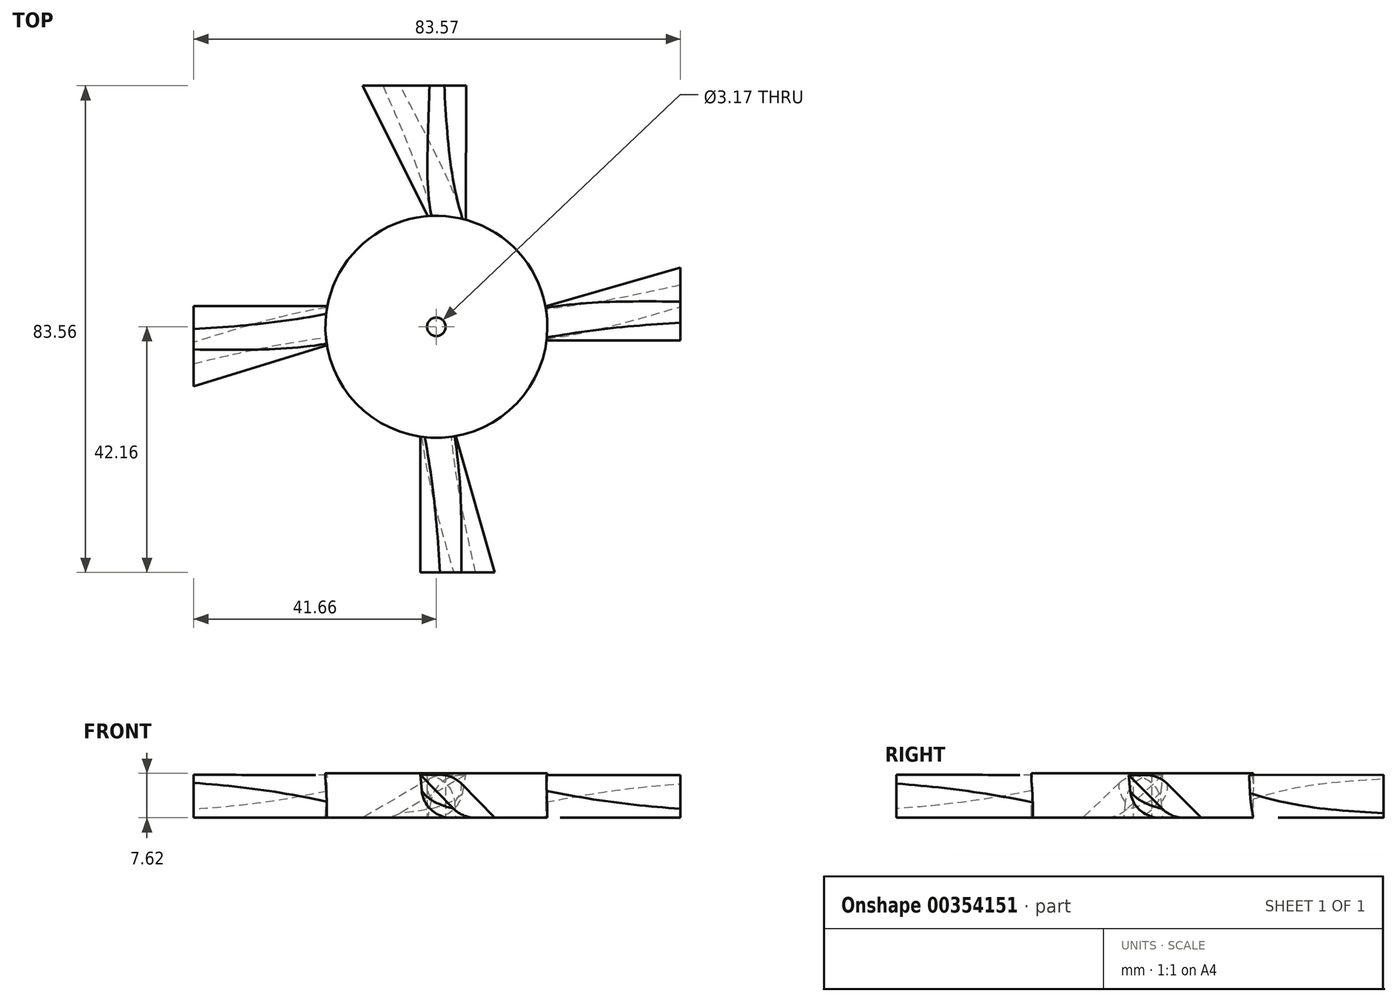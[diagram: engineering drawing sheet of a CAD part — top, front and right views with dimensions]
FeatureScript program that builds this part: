
annotation { "Feature Type Name" : "Feature", "Feature Type Description" : "" }
export const myFeature = defineFeature(function(context is Context, id is Id, definition is map)
    precondition{}
    {
        {
            var Q0;
            Q0=qCreatedBy(makeId("Top.planeOp"),FACE);
            var sketch = newSketch(context, id + "F0", { "sketchPlane" : qUnion([Q0])});
            skCircle(sketch, "E0", {"center": v(0, 0) * mm, "radius": 19.05 * mm});
            skCircle(sketch, "E1", {"center": v(0, 0) * mm, "radius": 1.59 * mm});
            skSolve(sketch);
        }
        {
            var Q0;
            Q0=makeQuery(id+"F0.imprint","IMPRINT",FACE,{"disambiguationData":[TD([[makeQuery(id+"F0.imprint","IMPRINT",EDGE,{"derivedFrom":sQuery(id+"F0.wireOp",EDGE,"E0")}),1.0]])]});
            extrude(context, id + "F1", {"entities" : qUnion([Q0]), "depth" : 7.62 * mm});
        }
        {
            var Q0;
            Q0=qCreatedBy(makeId("Front.planeOp"),FACE);
            cPlane(context, id + "F2", {"entities" : qUnion([Q0]), "cplaneType" : CPlaneType.OFFSET, "offset" : 16 * mm, "oppositeDirection" : true, "width" : 152.4 * mm, "height" : 152.4 * mm});
        }
        {
            var Q0;
            Q0=qCreatedBy(id+"F2.planeOp",FACE);
            var sketch = newSketch(context, id + "F3", { "sketchPlane" : qUnion([Q0])});
            skLineSegment(sketch, "E2.bottom", {"start": v(0, 7.29) * mm, "end": v(5.03, 7.29) * mm});
            skLineSegment(sketch, "E2.top", {"start": v(0, 0) * mm, "end": v(5.03, 0) * mm});
            skLineSegment(sketch, "E2.left", {"start": v(0, 7.29) * mm, "end": v(0, 0) * mm});
            skLineSegment(sketch, "E2.right", {"start": v(5.03, 7.29) * mm, "end": v(5.03, 0) * mm});
            skSolve(sketch);
        }
        {
            var Q0;
            Q0=qCreatedBy(id+"F2.planeOp",FACE);
            cPlane(context, id + "F4", {"entities" : qUnion([Q0]), "cplaneType" : CPlaneType.OFFSET, "offset" : 25.4 * mm, "oppositeDirection" : true, "width" : 152.4 * mm, "height" : 152.4 * mm});
        }
        {
            var Q0;
            Q0=qCreatedBy(id+"F4.planeOp",FACE);
            var sketch = newSketch(context, id + "F5", { "sketchPlane" : qUnion([Q0])});
            skLineSegment(sketch, "E3.bottom", {"start": v(5.1, 7.38) * mm, "end": v(0, 7.38) * mm});
            skLineSegment(sketch, "E3.top", {"start": v(-7.57, 0) * mm, "end": v(-12.68, 0) * mm});
            skLineSegment(sketch, "E3.left", {"start": v(5.1, 7.38) * mm, "end": v(-7.57, 0) * mm});
            skLineSegment(sketch, "E3.right", {"start": v(0, 7.38) * mm, "end": v(-12.68, 0) * mm});
            skSolve(sketch);
        }
        {
            var Q1;
            Q1 = qSketchRegion(id + "F3", true);
            var Q2;
            Q2 = qSketchRegion(id + "F5", true);
            loft(context, id + "F6", {"operationType" : NewBodyOperationType.ADD, "sheetProfilesArray" : [{ "sheetProfileEntities" : qUnion([Q1]) }, { "sheetProfileEntities" : qUnion([Q2]) }]});
        }
        {
            var Q0;
            Q0=makeQuery(id+"F6.opLoft","SWEPT_EDGE",EDGE,{"disambiguationData":[OSD([sQuery(id+"F3.wireOp",EDGE,"E2.bottom"),sQuery(id+"F3.wireOp",EDGE,"E2.left"),sQuery(id+"F5.wireOp",EDGE,"E3.bottom"),sQuery(id+"F5.wireOp",EDGE,"E3.right")])]});
            fillet(context, id + "F7", {"entities" : qUnion([Q0]), "radius" : 5.08 * mm, "tangentPropagation" : true, "allowEdgeOverflow" : false});
        }
        {
            var Q0;
            Q0=makeQuery(id+"F6.opLoft","SWEPT_EDGE",EDGE,{"disambiguationData":[OSD([sQuery(id+"F3.wireOp",EDGE,"E2.top"),sQuery(id+"F3.wireOp",EDGE,"E2.right"),sQuery(id+"F5.wireOp",EDGE,"E3.top"),sQuery(id+"F5.wireOp",EDGE,"E3.left")])]});
            fillet(context, id + "F8", {"entities" : qUnion([Q0]), "radius" : 5.08 * mm, "tangentPropagation" : true, "allowEdgeOverflow" : false});
        }
        {
            var Q0;
            Q0=qCreatedBy(makeId("Right.planeOp"),FACE);
            cPlane(context, id + "F9", {"entities" : qUnion([Q0]), "cplaneType" : CPlaneType.OFFSET, "offset" : 16.26 * mm, "oppositeDirection" : true, "width" : 152.4 * mm, "height" : 152.4 * mm});
        }
        {
            var Q0;
            Q0=qCreatedBy(id+"F9.planeOp",FACE);
            var sketch = newSketch(context, id + "F10", { "sketchPlane" : qUnion([Q0])});
            skLineSegment(sketch, "E4.bottom", {"start": v(3.55, 7.32) * mm, "end": v(-2.42, 7.32) * mm});
            skLineSegment(sketch, "E4.top", {"start": v(3.55, 0) * mm, "end": v(-2.42, 0) * mm});
            skLineSegment(sketch, "E4.left", {"start": v(3.55, 7.32) * mm, "end": v(3.55, 0) * mm});
            skLineSegment(sketch, "E4.right", {"start": v(-2.42, 7.32) * mm, "end": v(-2.42, 0) * mm});
            skSolve(sketch);
        }
        {
            var Q0;
            Q0=qCreatedBy(id+"F9.planeOp",FACE);
            cPlane(context, id + "F11", {"entities" : qUnion([Q0]), "cplaneType" : CPlaneType.OFFSET, "offset" : 25.4 * mm, "oppositeDirection" : true, "width" : 152.4 * mm, "height" : 152.4 * mm});
        }
        {
            var Q0;
            Q0=qCreatedBy(id+"F11.planeOp",FACE);
            var sketch = newSketch(context, id + "F12", { "sketchPlane" : qUnion([Q0])});
            skLineSegment(sketch, "E5.bottom", {"start": v(3.58, 7.37) * mm, "end": v(-2.42, 7.37) * mm});
            skLineSegment(sketch, "E5.top", {"start": v(-4.2, 0) * mm, "end": v(-10.2, 0) * mm});
            skLineSegment(sketch, "E5.left", {"start": v(3.58, 7.37) * mm, "end": v(-4.2, 0) * mm});
            skLineSegment(sketch, "E5.right", {"start": v(-2.42, 7.37) * mm, "end": v(-10.2, 0) * mm});
            skSolve(sketch);
        }
        {
            var Q1;
            Q1 = qSketchRegion(id + "F10", true);
            var Q2;
            Q2 = qSketchRegion(id + "F12", true);
            loft(context, id + "F13", {"operationType" : NewBodyOperationType.ADD, "sheetProfilesArray" : [{ "sheetProfileEntities" : qUnion([Q1]) }, { "sheetProfileEntities" : qUnion([Q2]) }]});
        }
        {
            var Q0;
            Q0=makeQuery(id+"F13.opLoft","SWEPT_EDGE",EDGE,{"disambiguationData":[OSD([sQuery(id+"F10.wireOp",EDGE,"E4.bottom"),sQuery(id+"F10.wireOp",EDGE,"E4.right"),sQuery(id+"F12.wireOp",EDGE,"E5.bottom"),sQuery(id+"F12.wireOp",EDGE,"E5.right")])]});
            fillet(context, id + "F14", {"entities" : qUnion([Q0]), "radius" : 5.08 * mm, "tangentPropagation" : true, "allowEdgeOverflow" : false});
        }
        {
            var Q0;
            Q0=makeQuery(id+"F13.opLoft","SWEPT_EDGE",EDGE,{"disambiguationData":[OSD([sQuery(id+"F10.wireOp",EDGE,"E4.top"),sQuery(id+"F10.wireOp",EDGE,"E4.left"),sQuery(id+"F12.wireOp",EDGE,"E5.top"),sQuery(id+"F12.wireOp",EDGE,"E5.left")])]});
            fillet(context, id + "F15", {"entities" : qUnion([Q0]), "radius" : 5.08 * mm, "tangentPropagation" : true, "allowEdgeOverflow" : false});
        }
        {
            var Q0;
            Q0=qCreatedBy(makeId("Front.planeOp"),FACE);
            cPlane(context, id + "F16", {"entities" : qUnion([Q0]), "cplaneType" : CPlaneType.OFFSET, "offset" : 16.76 * mm, "width" : 152.4 * mm, "height" : 152.4 * mm});
        }
        {
            var Q0;
            Q0=qCreatedBy(id+"F16.planeOp",FACE);
            var sketch = newSketch(context, id + "F17", { "sketchPlane" : qUnion([Q0])});
            skLineSegment(sketch, "E6.bottom", {"start": v(-2.73, 7.34) * mm, "end": v(2.75, 7.34) * mm});
            skLineSegment(sketch, "E6.top", {"start": v(-2.73, 0) * mm, "end": v(2.75, 0) * mm});
            skLineSegment(sketch, "E6.left", {"start": v(-2.73, 7.34) * mm, "end": v(-2.73, 0) * mm});
            skLineSegment(sketch, "E6.right", {"start": v(2.75, 7.34) * mm, "end": v(2.75, 0) * mm});
            skSolve(sketch);
        }
        {
            var Q0;
            Q0=qCreatedBy(id+"F16.planeOp",FACE);
            cPlane(context, id + "F18", {"entities" : qUnion([Q0]), "cplaneType" : CPlaneType.OFFSET, "offset" : 25.4 * mm, "width" : 152.4 * mm, "height" : 152.4 * mm});
        }
        {
            var Q0;
            Q0=qCreatedBy(id+"F18.planeOp",FACE);
            var sketch = newSketch(context, id + "F19", { "sketchPlane" : qUnion([Q0])});
            skLineSegment(sketch, "E7.bottom", {"start": v(-2.75, 7.38) * mm, "end": v(2.77, 7.38) * mm});
            skLineSegment(sketch, "E7.top", {"start": v(4.49, 0) * mm, "end": v(10.02, 0) * mm});
            skLineSegment(sketch, "E7.left", {"start": v(-2.75, 7.38) * mm, "end": v(4.49, 0) * mm});
            skLineSegment(sketch, "E7.right", {"start": v(2.77, 7.38) * mm, "end": v(10.02, 0) * mm});
            skSolve(sketch);
        }
        {
            var Q1;
            Q1 = qSketchRegion(id + "F17", true);
            var Q2;
            Q2 = qSketchRegion(id + "F19", true);
            loft(context, id + "F20", {"operationType" : NewBodyOperationType.ADD, "sheetProfilesArray" : [{ "sheetProfileEntities" : qUnion([Q1]) }, { "sheetProfileEntities" : qUnion([Q2]) }]});
        }
        {
            var Q0;
            Q0=makeQuery(id+"F20.opLoft","SWEPT_EDGE",EDGE,{"disambiguationData":[OSD([sQuery(id+"F17.wireOp",EDGE,"E6.top"),sQuery(id+"F17.wireOp",EDGE,"E6.left"),sQuery(id+"F19.wireOp",EDGE,"E7.top"),sQuery(id+"F19.wireOp",EDGE,"E7.left")])]});
            fillet(context, id + "F21", {"entities" : qUnion([Q0]), "radius" : 5.08 * mm, "tangentPropagation" : true, "allowEdgeOverflow" : false});
        }
        {
            var Q0;
            Q0=makeQuery(id+"F20.opLoft","SWEPT_EDGE",EDGE,{"disambiguationData":[OSD([sQuery(id+"F17.wireOp",EDGE,"E6.bottom"),sQuery(id+"F17.wireOp",EDGE,"E6.right"),sQuery(id+"F19.wireOp",EDGE,"E7.bottom"),sQuery(id+"F19.wireOp",EDGE,"E7.right")])]});
            fillet(context, id + "F22", {"entities" : qUnion([Q0]), "radius" : 5.08 * mm, "tangentPropagation" : true, "allowEdgeOverflow" : false});
        }
        {
            var Q0;
            Q0=qCreatedBy(makeId("Right.planeOp"),FACE);
            cPlane(context, id + "F23", {"entities" : qUnion([Q0]), "cplaneType" : CPlaneType.OFFSET, "offset" : 16.5 * mm, "width" : 152.4 * mm, "height" : 152.4 * mm});
        }
        {
            var Q0;
            Q0=qCreatedBy(id+"F23.planeOp",FACE);
            var sketch = newSketch(context, id + "F24", { "sketchPlane" : qUnion([Q0])});
            skLineSegment(sketch, "E8.bottom", {"start": v(-2.32, 7.3) * mm, "end": v(2.85, 7.3) * mm});
            skLineSegment(sketch, "E8.top", {"start": v(-2.32, 0) * mm, "end": v(2.85, 0) * mm});
            skLineSegment(sketch, "E8.left", {"start": v(-2.32, 7.3) * mm, "end": v(-2.32, 0) * mm});
            skLineSegment(sketch, "E8.right", {"start": v(2.85, 7.3) * mm, "end": v(2.85, 0) * mm});
            skSolve(sketch);
        }
        {
            var Q0;
            Q0=qCreatedBy(id+"F23.planeOp",FACE);
            cPlane(context, id + "F25", {"entities" : qUnion([Q0]), "cplaneType" : CPlaneType.OFFSET, "offset" : 25.4 * mm, "width" : 152.4 * mm, "height" : 152.4 * mm});
        }
        {
            var Q0;
            Q0=qCreatedBy(id+"F25.planeOp",FACE);
            var sketch = newSketch(context, id + "F26", { "sketchPlane" : qUnion([Q0])});
            skLineSegment(sketch, "E9.bottom", {"start": v(-2.32, 7.32) * mm, "end": v(2.83, 7.32) * mm});
            skLineSegment(sketch, "E9.top", {"start": v(4.99, 0) * mm, "end": v(10.14, 0) * mm});
            skLineSegment(sketch, "E9.left", {"start": v(-2.32, 7.32) * mm, "end": v(4.99, 0) * mm});
            skLineSegment(sketch, "E9.right", {"start": v(2.83, 7.32) * mm, "end": v(10.14, 0) * mm});
            skSolve(sketch);
        }
        {
            var Q1;
            Q1 = qSketchRegion(id + "F24", true);
            var Q2;
            Q2 = qSketchRegion(id + "F26", true);
            loft(context, id + "F27", {"operationType" : NewBodyOperationType.ADD, "sheetProfilesArray" : [{ "sheetProfileEntities" : qUnion([Q1]) }, { "sheetProfileEntities" : qUnion([Q2]) }]});
        }
        {
            var Q0;
            Q0=makeQuery(id+"F27.opLoft","SWEPT_EDGE",EDGE,{"disambiguationData":[OSD([sQuery(id+"F24.wireOp",EDGE,"E8.top"),sQuery(id+"F24.wireOp",EDGE,"E8.left"),sQuery(id+"F26.wireOp",EDGE,"E9.top"),sQuery(id+"F26.wireOp",EDGE,"E9.left")])]});
            fillet(context, id + "F28", {"entities" : qUnion([Q0]), "radius" : 5.08 * mm, "tangentPropagation" : true, "allowEdgeOverflow" : false});
        }
        {
            var Q0;
            Q0=makeQuery(id+"F27.opLoft","SWEPT_EDGE",EDGE,{"disambiguationData":[OSD([sQuery(id+"F24.wireOp",EDGE,"E8.bottom"),sQuery(id+"F24.wireOp",EDGE,"E8.right"),sQuery(id+"F26.wireOp",EDGE,"E9.bottom"),sQuery(id+"F26.wireOp",EDGE,"E9.right")])]});
            fillet(context, id + "F29", {"entities" : qUnion([Q0]), "radius" : 5.08 * mm, "tangentPropagation" : true, "allowEdgeOverflow" : false});
        }
    });
